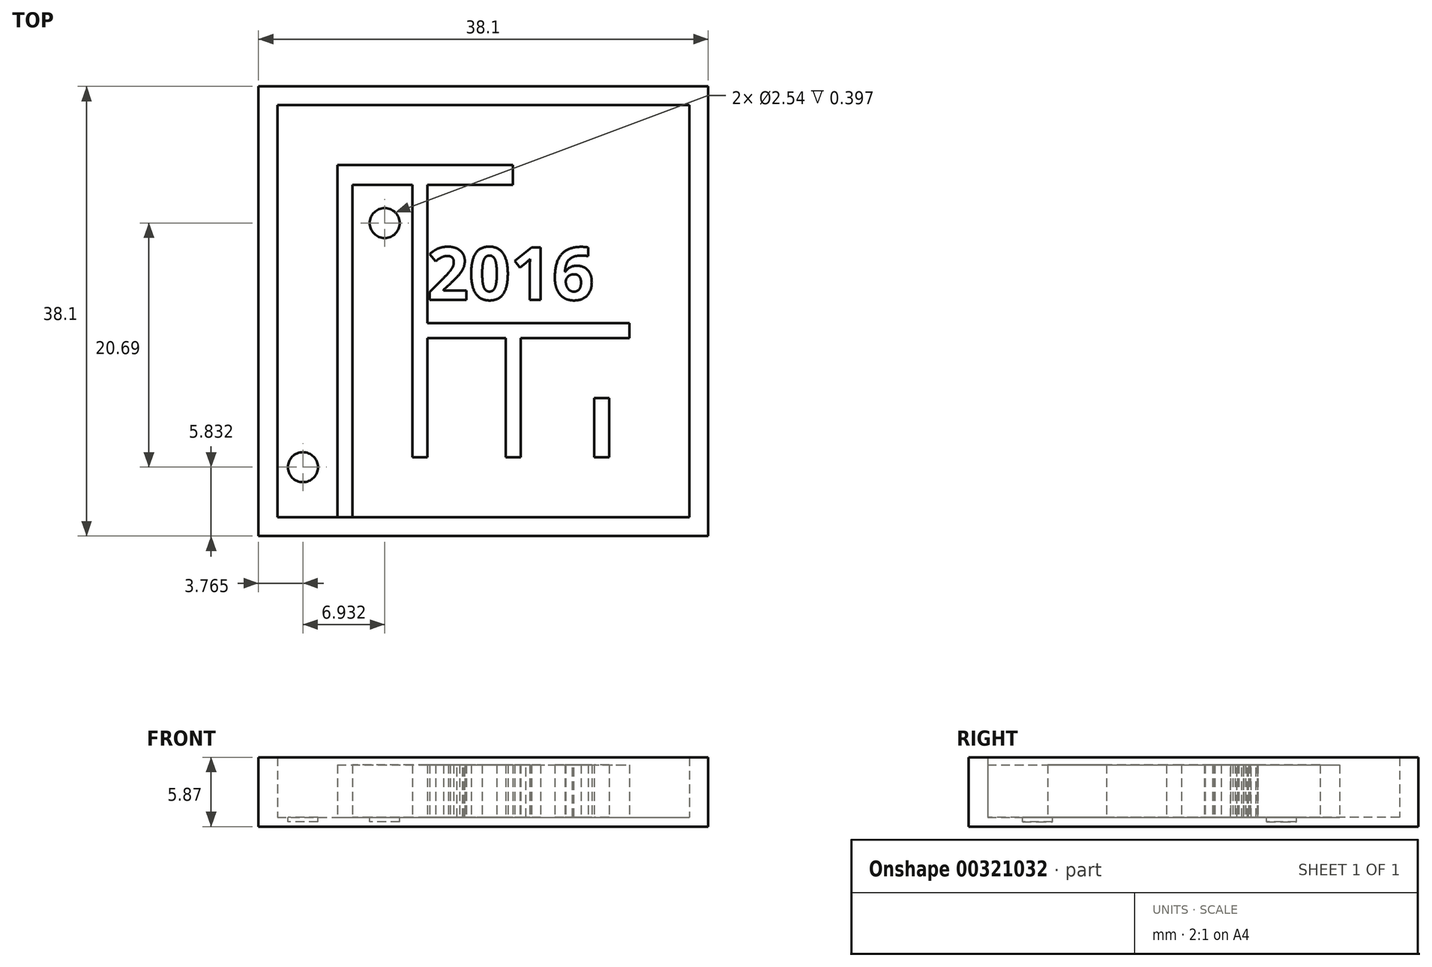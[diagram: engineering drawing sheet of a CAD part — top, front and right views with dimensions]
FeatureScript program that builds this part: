
annotation { "Feature Type Name" : "Feature", "Feature Type Description" : "" }
export const myFeature = defineFeature(function(context is Context, id is Id, definition is map)
    precondition{}
    {
        {
            var Q0;
            Q0=qCreatedBy(makeId("Top.planeOp"),FACE);
            var sketch = newSketch(context, id + "F0", { "sketchPlane" : qUnion([Q0])});
            skLineSegment(sketch, "E0.bottom", {"start": v(-14.26, 7.33) * mm, "end": v(23.84, 7.33) * mm});
            skLineSegment(sketch, "E0.top", {"start": v(-14.26, -30.77) * mm, "end": v(23.84, -30.77) * mm});
            skLineSegment(sketch, "E0.left", {"start": v(-14.26, 7.33) * mm, "end": v(-14.26, -30.77) * mm});
            skLineSegment(sketch, "E0.right", {"start": v(23.84, 7.33) * mm, "end": v(23.84, -30.77) * mm});
            skSolve(sketch);
        }
        {
            var Q0;
            Q0=makeQuery(id+"F0.imprint","IMPRINT",FACE,{"disambiguationData":[TD([[makeQuery(id+"F0.imprint","IMPRINT",EDGE,{"derivedFrom":sQuery(id+"F0.wireOp",EDGE,"E0.bottom")}),-1.0]])]});
            extrude(context, id + "F1", {"entities" : qUnion([Q0]), "depth" : 0.8 * mm});
        }
        {
            var Q0;
            Q0=makeQuery(id+"F1.opExtrude","CAP_FACE",FACE,{"disambiguationData":[OSD([sQuery(id+"F0.wireOp",EDGE,"E0.bottom"),sQuery(id+"F0.wireOp",EDGE,"E0.top"),sQuery(id+"F0.wireOp",EDGE,"E0.left"),sQuery(id+"F0.wireOp",EDGE,"E0.right")])],"isStart":false});
            var sketch = newSketch(context, id + "F2", { "sketchPlane" : qUnion([Q0])});
            skLineSegment(sketch, "E1.0", {"start": v(-12.66, 5.73) * mm, "end": v(22.24, 5.73) * mm});
            skLineSegment(sketch, "E1.1", {"start": v(-12.66, 5.73) * mm, "end": v(-12.66, -29.16) * mm});
            skLineSegment(sketch, "E1.2", {"start": v(-12.66, -29.16) * mm, "end": v(22.24, -29.16) * mm});
            skLineSegment(sketch, "E1.3", {"start": v(22.24, 5.73) * mm, "end": v(22.24, -29.16) * mm});
            skSolve(sketch);
        }
        {
            var Q0;
            Q0=makeQuery(id+"F2.imprint","IMPRINT",FACE,{"disambiguationData":[TD([[makeQuery(id+"F2.imprint","IMPRINT",EDGE,{"derivedFrom":sQuery(id+"F2.wireOp",EDGE,"E1.0")}),1.0]])]});
            extrude(context, id + "F3", {"entities" : qUnion([Q0]), "operationType" : NewBodyOperationType.ADD, "depth" : 5.08 * mm});
        }
        {
            var Q0;
            Q0=makeQuery(id+"F1.opExtrude","CAP_FACE",FACE,{"disambiguationData":[OSD([sQuery(id+"F0.wireOp",EDGE,"E0.bottom"),sQuery(id+"F0.wireOp",EDGE,"E0.top"),sQuery(id+"F0.wireOp",EDGE,"E0.left"),sQuery(id+"F0.wireOp",EDGE,"E0.right")])],"isStart":false});
            var sketch = newSketch(context, id + "F4", { "sketchPlane" : qUnion([Q0])});
            skLineSegment(sketch, "E2.bottom", {"start": v(-7.58, -29.16) * mm, "end": v(-6.3, -29.16) * mm});
            skLineSegment(sketch, "E2.top", {"start": v(-7.58, 0.65) * mm, "end": v(-6.3, 0.65) * mm});
            skLineSegment(sketch, "E2.left", {"start": v(-7.58, -29.16) * mm, "end": v(-7.58, 0.65) * mm});
            skLineSegment(sketch, "E2.right", {"start": v(-6.3, -29.16) * mm, "end": v(-6.3, 0.65) * mm});
            skPoint(sketch, "E3.end.orphan", {"position": v(3.66, 0.65) * mm});
            skPoint(sketch, "E4.end.orphan", {"position": v(0.04, 0.65) * mm});
            skLineSegment(sketch, "E5.bottom", {"start": v(-1.23, 0.65) * mm, "end": v(3.66, 0.65) * mm});
            skLineSegment(sketch, "E5.top", {"start": v(-1.23, 0.65) * mm, "end": v(7.29, 0.65) * mm});
            skLineSegment(sketch, "E5.left", {"start": v(-6.3, 0.65) * mm, "end": v(-6.3, 0.65) * mm});
            skLineSegment(sketch, "E5.right", {"start": v(7.29, -1) * mm, "end": v(7.29, 0.65) * mm});
            skPoint(sketch, "E6.firstSnap0", {"position": v(5.66, -0.17) * mm});
            skPoint(sketch, "E7.top.end.orphan", {"position": v(14.47, 0.65) * mm});
            skPoint(sketch, "E8.end.orphan", {"position": v(10.93, -0.17) * mm});
            skPoint(sketch, "E9.trimOffspring.start.orphan", {"position": v(7.29, -20.45) * mm});
            skPoint(sketch, "E10.top.end.orphan", {"position": v(17.08, -23.34) * mm});
            skPoint(sketch, "E11.start.orphan", {"position": v(17.08, -26.42) * mm});
            skPoint(sketch, "E10.bottom.start.orphan", {"position": v(0.67, -20.45) * mm});
            skPoint(sketch, "E12.right.start.orphan", {"position": v(4.02, 0.65) * mm});
            skLineSegment(sketch, "E13.top", {"start": v(0.04, -24.08) * mm, "end": v(-1.23, -24.08) * mm});
            skLineSegment(sketch, "E13.left", {"start": v(0.04, -1) * mm, "end": v(0.04, -12.73) * mm});
            skLineSegment(sketch, "E13.right", {"start": v(-1.23, -1.37) * mm, "end": v(-1.23, -24.08) * mm});
            skLineSegment(sketch, "E14.bottom", {"start": v(0.04, -12.73) * mm, "end": v(17.16, -12.73) * mm});
            skLineSegment(sketch, "E14.top", {"start": v(0.04, -14) * mm, "end": v(6.7, -14) * mm});
            skLineSegment(sketch, "E14.left", {"start": v(-1.23, -12.73) * mm, "end": v(-1.23, -14) * mm});
            skLineSegment(sketch, "E14.right", {"start": v(17.16, -12.73) * mm, "end": v(17.16, -14) * mm});
            skLineSegment(sketch, "E15.bottom", {"start": v(7.97, -12.73) * mm, "end": v(5.66, -12.73) * mm});
            skLineSegment(sketch, "E15.top", {"start": v(8.36, -29.16) * mm, "end": v(5.66, -29.16) * mm});
            skLineSegment(sketch, "E16", {"start": v(6.7, -14) * mm, "end": v(6.7, -24.08) * mm});
            skLineSegment(sketch, "E17", {"start": v(7.97, -14) * mm, "end": v(7.97, -24.08) * mm});
            skPoint(sketch, "E18.orphan", {"position": v(-1.23, -1.37) * mm});
            skLineSegment(sketch, "E19.bottom", {"start": v(15.45, -19.08) * mm, "end": v(14.18, -19.08) * mm});
            skLineSegment(sketch, "E19.top", {"start": v(15.45, -24.08) * mm, "end": v(14.18, -24.08) * mm});
            skLineSegment(sketch, "E19.left", {"start": v(15.45, -19.08) * mm, "end": v(15.45, -24.08) * mm});
            skLineSegment(sketch, "E19.right", {"start": v(14.18, -19.08) * mm, "end": v(14.18, -24.08) * mm});
            skText(sketch, "E20", { "text": "2016", "fontName": "OpenSans-Bold.ttf"});
            skLineSegment(sketch, "E21", {"start": v(6.7, -24.08) * mm, "end": v(7.97, -24.08) * mm});
            skLineSegment(sketch, "E22", {"start": v(7.29, -1) * mm, "end": v(0.04, -1) * mm});
            skLineSegment(sketch, "E23", {"start": v(-6.3, 0.65) * mm, "end": v(-1.23, 0.65) * mm});
            skLineSegment(sketch, "E24", {"start": v(0.04, -1) * mm, "end": v(-6.3, -1) * mm});
            skLineSegment(sketch, "E25", {"start": v(-1.23, -1.37) * mm, "end": v(-1.23, -1) * mm});
            skLineSegment(sketch, "E26.trimOffspring", {"start": v(0.04, -14) * mm, "end": v(0.04, -24.08) * mm});
            skLineSegment(sketch, "E27.trimOffspring", {"start": v(7.97, -14) * mm, "end": v(17.16, -14) * mm});
            const initialGuessF4  = {"E20": [0, -0.01075, 1, 0, 0.00447]};
            skSetInitialGuess(sketch, initialGuessF4);
            skSolve(sketch);
        }
        {
            var Q0;
            Q0=makeQuery(id+"F4.imprint","IMPRINT",FACE,{"disambiguationData":[TD([[makeQuery(id+"F4.imprint","IMPRINT",EDGE,{"derivedFrom":sQuery(id+"F4.wireOp",EDGE,"E2.bottom")}),1.0]])]});
            extrude(context, id + "F5", {"entities" : qUnion([Q0]), "operationType" : NewBodyOperationType.ADD, "depth" : 4.44 * mm});
        }
        {
            var Q0;
            Q0=makeQuery(id+"F2.imprint","IMPRINT",FACE,{"disambiguationData":[TD([[makeQuery(id+"F2.imprint","IMPRINT",EDGE,{"derivedFrom":sQuery(id+"F2.wireOp",EDGE,"E1.0")}),-1.0]])]});
            var sketch = newSketch(context, id + "F6", { "sketchPlane" : qUnion([Q0])});
            skCircle(sketch, "E28", {"center": v(-10.5, -24.94) * mm, "radius": 1.27 * mm});
            skCircle(sketch, "E29", {"center": v(-3.56, -4.25) * mm, "radius": 1.27 * mm});
            skSolve(sketch);
        }
        {
            var Q0;
            Q0 = qSketchRegion(id + "F6", true);
            extrude(context, id + "F7", {"entities" : qUnion([Q0]), "operationType" : NewBodyOperationType.REMOVE, "oppositeDirection" : true, "depth" : 0.4 * mm});
        }
        {
            var Q0;
            Q0 = qSketchRegion(id + "F4", true);
            extrude(context, id + "F8", {"entities" : qUnion([Q0]), "operationType" : NewBodyOperationType.ADD, "depth" : 4.44 * mm});
        }
        {
            var Q0;
            Q0 = qSketchRegion(id + "F4", true);
            extrude(context, id + "F9", {"entities" : qUnion([Q0]), "operationType" : NewBodyOperationType.ADD, "depth" : 4.44 * mm});
        }
        {
            var Q0;
            Q0 = qSketchRegion(id + "F4", true);
            extrude(context, id + "F10", {"entities" : qUnion([Q0]), "operationType" : NewBodyOperationType.ADD, "depth" : 4.44 * mm});
        }
    });
